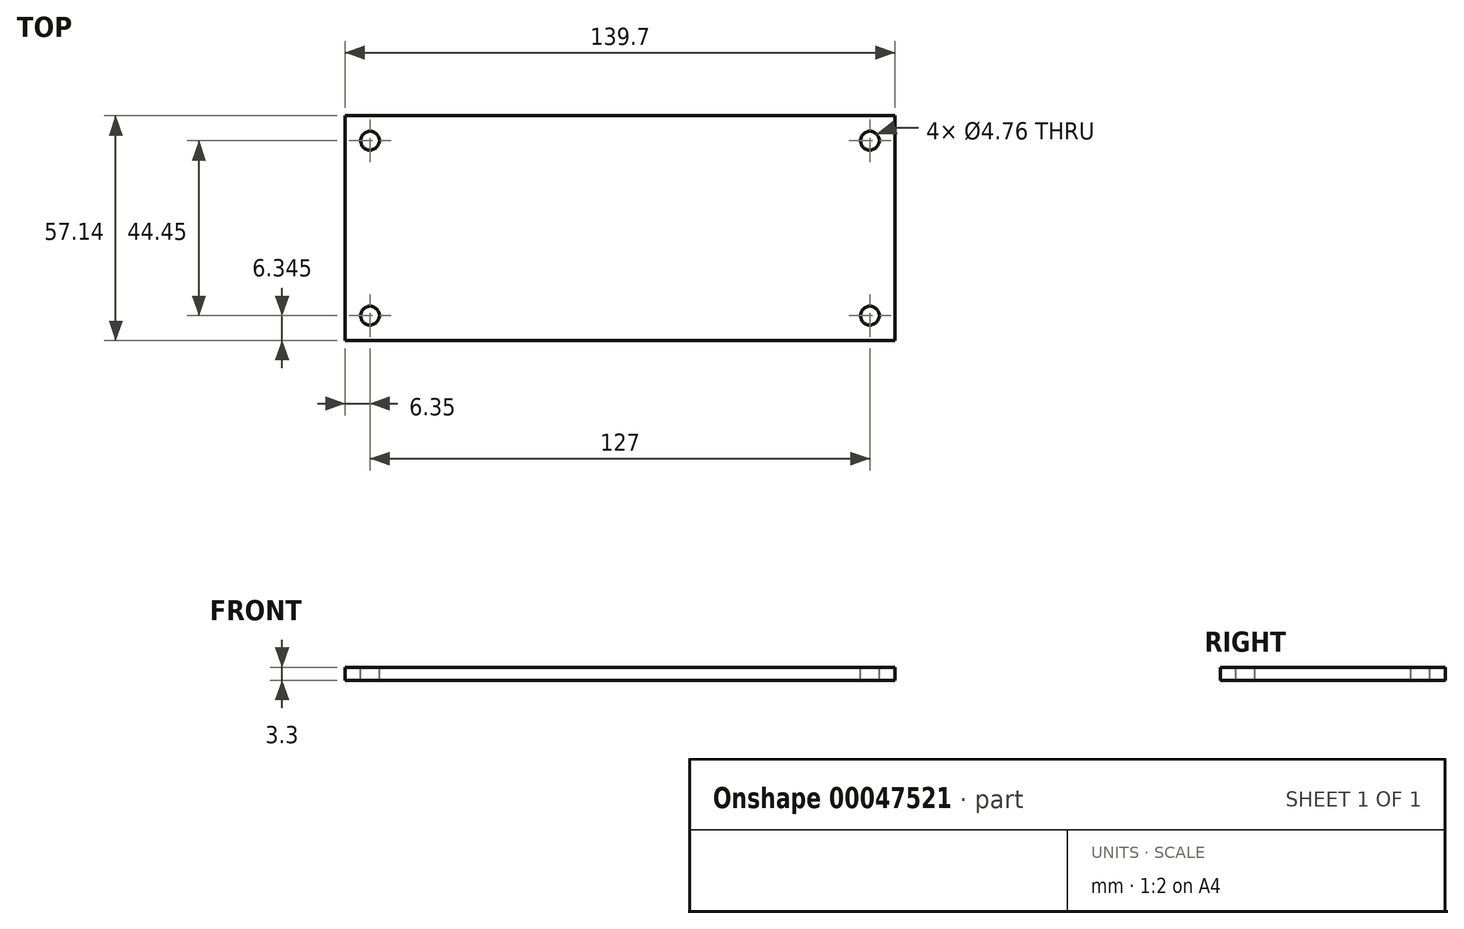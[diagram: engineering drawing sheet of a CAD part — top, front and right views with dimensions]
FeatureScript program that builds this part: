
annotation { "Feature Type Name" : "Feature", "Feature Type Description" : "" }
export const myFeature = defineFeature(function(context is Context, id is Id, definition is map)
    precondition{}
    {
        {
            var Q0;
            Q0=qCreatedBy(makeId("Top.planeOp"),FACE);
            var sketch = newSketch(context, id + "F0", { "sketchPlane" : qUnion([Q0])});
            skLineSegment(sketch, "E0.rect.bottom", {"start": v(-69.85, 28.58) * mm, "end": v(69.85, 28.58) * mm});
            skLineSegment(sketch, "E0.rect.top", {"start": v(-69.85, -28.58) * mm, "end": v(69.85, -28.58) * mm});
            skLineSegment(sketch, "E0.rect.left", {"start": v(-69.85, 28.58) * mm, "end": v(-69.85, -28.57) * mm});
            skLineSegment(sketch, "E0.rect.right", {"start": v(69.85, 28.58) * mm, "end": v(69.85, -28.57) * mm});
            skPoint(sketch, "E0.rect.middle", {"position": v(0, 0) * mm});
            skSolve(sketch);
        }
        {
            var Q0;
            Q0 = qSketchRegion(id + "F0", true);
            extrude(context, id + "F1", {"entities" : qUnion([Q0]), "endBound" : BoundingType.SYMMETRIC, "depth" : 3.3 * mm});
        }
        {
            var Q0;
            Q0=qCreatedBy(makeId("Top.planeOp"),FACE);
            var sketch = newSketch(context, id + "F2", { "sketchPlane" : qUnion([Q0])});
            skCircle(sketch, "E1", {"center": v(-63.5, 22.23) * mm, "radius": 2.38 * mm});
            skSolve(sketch);
        }
        {
            var Q0;
            Q0 = qSketchRegion(id + "F2", true);
            extrude(context, id + "F3", {"entities" : qUnion([Q0]), "operationType" : NewBodyOperationType.REMOVE, "endBound" : BoundingType.SYMMETRIC, "oppositeDirection" : true, "depth" : 3.3 * mm});
        }
        {
            var Q0;
            Q0=qCreatedBy(makeId("Top.planeOp"),FACE);
            var sketch = newSketch(context, id + "F4", { "sketchPlane" : qUnion([Q0])});
            skCircle(sketch, "E2", {"center": v(63.5, 22.23) * mm, "radius": 2.38 * mm});
            skSolve(sketch);
        }
        {
            var Q0;
            Q0 = qSketchRegion(id + "F4", true);
            extrude(context, id + "F5", {"entities" : qUnion([Q0]), "operationType" : NewBodyOperationType.REMOVE, "endBound" : BoundingType.SYMMETRIC, "oppositeDirection" : true, "depth" : 3.3 * mm});
        }
        {
            var Q0;
            Q0=qCreatedBy(makeId("Top.planeOp"),FACE);
            var sketch = newSketch(context, id + "F6", { "sketchPlane" : qUnion([Q0])});
            skCircle(sketch, "E3", {"center": v(-63.5, -22.23) * mm, "radius": 2.38 * mm});
            skSolve(sketch);
        }
        {
            var Q0;
            Q0 = qSketchRegion(id + "F6", true);
            extrude(context, id + "F7", {"entities" : qUnion([Q0]), "operationType" : NewBodyOperationType.REMOVE, "endBound" : BoundingType.SYMMETRIC, "oppositeDirection" : true, "depth" : 3.3 * mm});
        }
        {
            var Q0;
            Q0=qCreatedBy(makeId("Top.planeOp"),FACE);
            var sketch = newSketch(context, id + "F8", { "sketchPlane" : qUnion([Q0])});
            skCircle(sketch, "E4", {"center": v(63.5, -22.23) * mm, "radius": 2.38 * mm});
            skSolve(sketch);
        }
        {
            var Q0;
            Q0 = qSketchRegion(id + "F8", true);
            extrude(context, id + "F9", {"entities" : qUnion([Q0]), "operationType" : NewBodyOperationType.REMOVE, "endBound" : BoundingType.SYMMETRIC, "oppositeDirection" : true, "depth" : 3.3 * mm});
        }
    });
